# Revit family: CDR-ZYA7, ZX08, ZY07, XY07, XYA7
name_source: partatom
category: Mechanical Equipment
revit_build: Autodesk Revit 2018 (Build: 20170630_0700(x64)
units: mm (PartAtom-declared; Revit-internal decimal feet)

## family parameters
Always vertical = Yes
Cut with Voids When Loaded = No
Part Type = Normal
Room Calculation Point = No
Round Connector Dimension = Use Diameter
Shared = No
Work Plane-Based = No

## types (2) — shared parameters
Cabinet Base Thickness = 3.060"
Clearance Back = 36.000"
Clearance Front = 48.000"
Clearance Left = 12.000"
Clearance Right = 18.000"
Clearance Top = 72.000"
Compressor Locked Rotor Current = 0 A
Compressor Maximum Continuous Current = 0 A
Compressor Running Load Current = 0 A
Compressor Size = 0
Compressor Type = Scroll
Condensate Drain Connection Diameter = 1"
Condenser Coil Rows = 1
Condenser Coils Fins per Inch = 23
Condenser Fan Diameter = 22.000"
Condenser Fan Drive Type = Direct
Condenser Fan Full Load Current = 0 A
Condenser Fan HP = 0 VA
Condenser Fan Quantity = 2
Convenience Outlet Full Load Current = 0 A
Curb Length = 81.750"
Curb Material = Metal - JCI - Steel - Galvanized With Wood Nailer
Curb Thicknes = 1.750"
Curb Width = 53.500"
Evaporator Coil Fins per Inch = 15
Evaporator Coil Row Count = 3
Exhaust Air Flow = 0 CFM
Family Revision Date = 10/31/2017
Filter Size and Quantity = (16 x 20 x 2) - 4
Filter Type = 2"
Frame Finish = Paint - JCI - Powder Coated - Galvanized Steel
Gas Connection Diameter = 1"
Gas Heating Performance MBH Input = 0 Btu/h
Gas Heating Performance MBH Output = 0 Btu/h
Height = 40.560"
Length = 87.180"
Manufacturer = Johnson Controls, Inc.
Maximum Overcurrent Protection = 0 A
Number of Poles = 3
OmniClass Number = 23.75.10.24.21.27.14
OmniClass Title = Packaged Rooftop Air Conditioning Units
Power Factor = 1
Refrigerant Used = R-410A
Return Air Connection Height = 13"
Return Air Connection Height (Optional) = 34"
Return Air Connection Width = 36"
Return Air Connection Width (Optional) = 13"
Supply Air Connection Height = 29"
Supply Air Connection Height (Optional) = 14"
Supply Air Connection Width = 14"
Supply Air Connection Width (Optional) = 28"
Supply Fan Full Load Current = 0 A
Supply Fan HP = 0 VA
URL = www.johnsoncontrols.com
Voltage = 208 V
Width = 61.690"
zero-valued in all types: Energy Efficiency Rating, Integrated Part Load Value

## per-type parameters (varying)
| type | Compressor Quantity | Description | Model | Nominal Cooling Capacity | Operating Weight | Refrigerant Charge System One | Refrigerant Charge System Two |
| ZX08 - 7.5 Ton | 2 | CDR Packaged Unit - 7.5 Ton Unit | ZX08 | 7.5 ton | 791.00 lb | 4.50 lb | 4.75 lb |
| ZY07 - 6 Ton | 1 | CDR Packaged Unit - 6 Ton Unit | ZY07 | 6.0 ton | 734.00 lb | 8.50 lb | 0.00 lb |

## geometry (parser evidence)
native form markers: Sweep x7
no freeform markers — native parametric forms only
